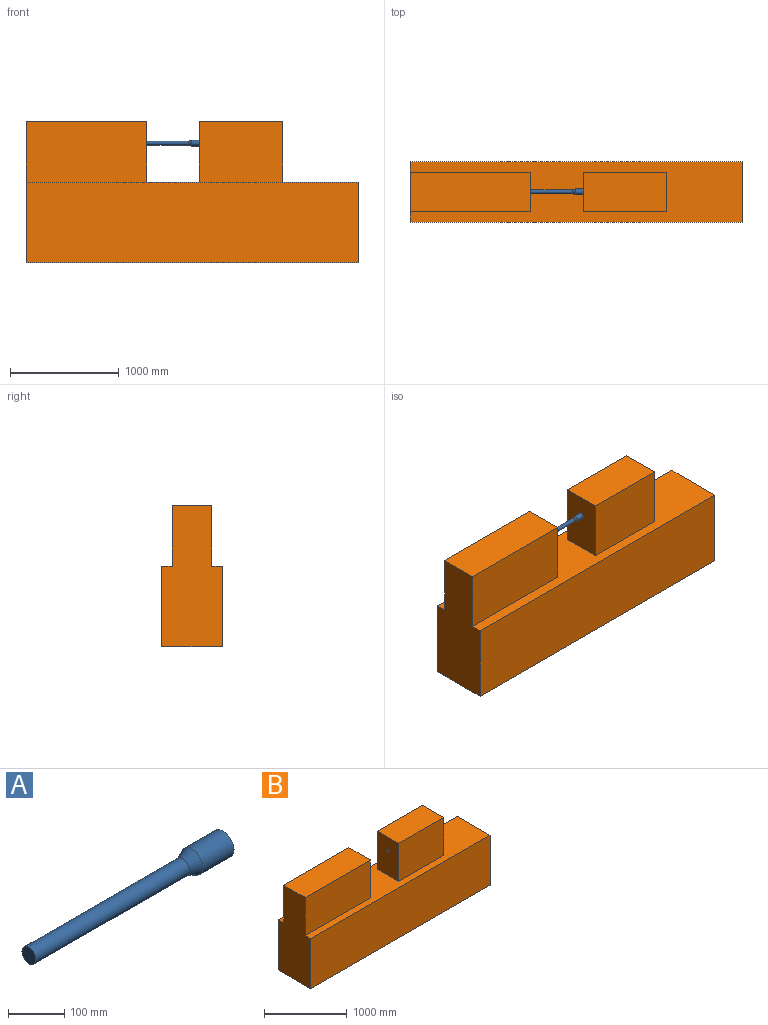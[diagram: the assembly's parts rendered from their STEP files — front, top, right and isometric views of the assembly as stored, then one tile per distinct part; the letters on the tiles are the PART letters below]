
ASSEMBLY  parts=2 mates=1
PART A: 5 faces, bbox 488x54x54 mm
  f0: plane 35x35mm, normal (-1,0,0), area 962.1mm2, adj f4
  f1: plane 54x54mm, normal (1,0,0), area 2290.2mm2, adj f2
  f2: cylinder r=27mm len=78mm, axis (1,0,0), area 13232.4mm2, adj f1,f3
  f3: cone r=17.5mm half-angle=21.6deg, axis (1,0,0), area 3608.5mm2, adj f2,f4
  f4: cylinder r=17.5mm len=386mm, axis (1,0,0), area 42442.9mm2, adj f0,f3
PART B: 19 faces, bbox 3059x560x1300 mm
  f0: plane 3059x560mm, normal (0,0,1), area 1026146.5mm2, adj f1,f2,f3,f4,f6,f7,f8,f10
  f1: plane 740x560mm, normal (1,0,0), area 414400mm2, adj f0,f2,f4,f5
  f2: plane 3059x740mm, normal (0,1,0), area 2263660mm2, adj f0,f1,f3,f5
  f3: plane 1300x560mm, normal (-1,0,0), area 618800mm2, adj f0,f2,f4,f5,f6,f7,f9
  f4: plane 3059x740mm, normal (0,-1,0), area 2263660mm2, adj f0,f1,f3,f5
  f5: plane 3059x560mm, normal (0,0,-1), area 1713040mm2, adj f1,f2,f3,f4
  f6: plane 1112.2x560mm, normal (0,1,0), area 622832mm2, adj f0,f3,f8,f9
  f7: plane 1112.2x560mm, normal (0,-1,0), area 622832mm2, adj f0,f3,f8,f9
  f8: plane 560x365mm, normal (1,0,0), area 203382.1mm2, adj f0,f6,f7,f9,f17
  f9: plane 1112.2x365mm, normal (0,0,1), area 405953mm2, adj f3,f6,f7,f8
  f10: plane 769.7x560mm, normal (0,1,0), area 431032mm2, adj f0,f11,f13,f14
  f11: plane 560x365mm, normal (-1,0,0), area 203382.1mm2, adj f0,f10,f12,f14,f16
  f12: plane 769.7x560mm, normal (0,-1,0), area 431032mm2, adj f0,f11,f13,f14
  f13: plane 560x365mm, normal (1,0,0), area 204400mm2, adj f0,f10,f12,f14
  f14: plane 769.7x365mm, normal (0,0,1), area 280940.5mm2, adj f10,f11,f12,f13
  f15: plane 36x36mm, normal (-1,0,0), area 1017.9mm2, adj f16
  f16: cylinder r=18mm len=36mm, axis (-1,0,0), area 3947.1mm2, adj f11,f15
  f17: cylinder r=18mm len=84mm, axis (-1,0,0), area 9500.2mm2, adj f8,f18
  f18: plane 36x36mm, normal (1,0,0), area 1017.9mm2, adj f17
PLACE A t=(-417.3,0,1100)mm
PLACE B at identity fixed
MATE revolute A.f2 <-> B.f16  axis (1,0,0) through (-417.3,0,1100)mm
